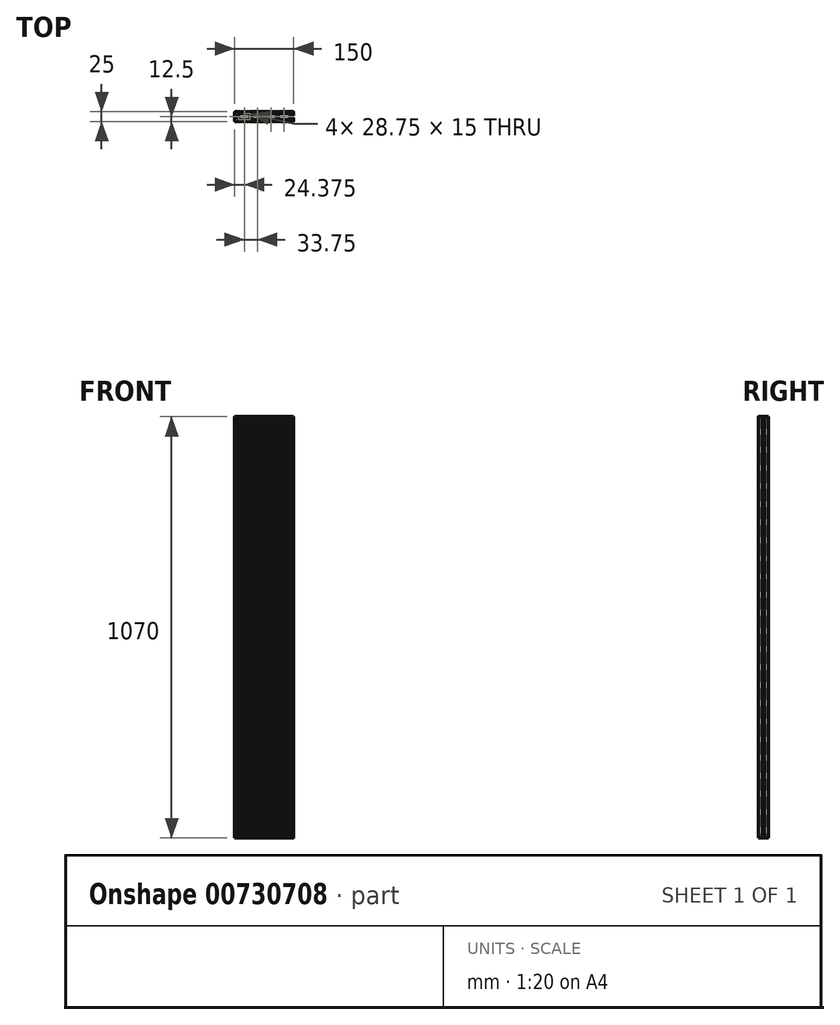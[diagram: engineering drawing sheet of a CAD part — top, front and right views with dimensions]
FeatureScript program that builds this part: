
annotation { "Feature Type Name" : "Feature", "Feature Type Description" : "" }
export const myFeature = defineFeature(function(context is Context, id is Id, definition is map)
    precondition{}
    {
        {
            var Q0;
            Q0=qCreatedBy(makeId("Top.planeOp"),FACE);
            var sketch = newSketch(context, id + "F0", { "sketchPlane" : qUnion([Q0])});
            skLineSegment(sketch, "E0", {"start": v(0, 26.25) * mm, "end": v(0, -33.75) * mm, "construction": true});
            skLineSegment(sketch, "E1", {"start": v(-31.25, 0) * mm, "end": v(28.53, 0) * mm, "construction": true});
            skLineSegment(sketch, "E2", {"start": v(0, 12.5) * mm, "end": v(-75, 12.5) * mm});
            skLineSegment(sketch, "E3", {"start": v(-75, 12.5) * mm, "end": v(-75, 2.5) * mm});
            skLineSegment(sketch, "E4", {"start": v(-75, 2.5) * mm, "end": v(-70, 2.5) * mm});
            skLineSegment(sketch, "E5", {"start": v(-70, 2.5) * mm, "end": v(-70, 0) * mm});
            skLineSegment(sketch, "E6", {"start": v(-65, 0) * mm, "end": v(-65, 7.5) * mm});
            skLineSegment(sketch, "E7", {"start": v(-65, 7.5) * mm, "end": v(-36.25, 7.5) * mm});
            skLineSegment(sketch, "E8", {"start": v(-36.25, 7.5) * mm, "end": v(-36.25, 0) * mm});
            skLineSegment(sketch, "E9", {"start": v(-31.25, 0) * mm, "end": v(-31.25, 7.5) * mm});
            skLineSegment(sketch, "E10", {"start": v(-31.25, 7.5) * mm, "end": v(-2.5, 7.5) * mm});
            skLineSegment(sketch, "E11", {"start": v(-2.5, 7.5) * mm, "end": v(-2.5, 0) * mm});
            skLineSegment(sketch, "E12.MirrorCS", {"start": v(75, 12.5) * mm, "end": v(75, 2.5) * mm});
            skLineSegment(sketch, "E13.MirrorCS", {"start": v(75, 2.5) * mm, "end": v(70, 2.5) * mm});
            skLineSegment(sketch, "E14.MirrorCS", {"start": v(70, 2.5) * mm, "end": v(70, 0) * mm});
            skLineSegment(sketch, "E15.MirrorCS", {"start": v(65, 0) * mm, "end": v(65, 7.5) * mm});
            skLineSegment(sketch, "E16.MirrorCS", {"start": v(65, 7.5) * mm, "end": v(36.25, 7.5) * mm});
            skLineSegment(sketch, "E17.MirrorCS", {"start": v(36.25, 7.5) * mm, "end": v(36.25, 0) * mm});
            skLineSegment(sketch, "E18.MirrorCS", {"start": v(0, 12.5) * mm, "end": v(75, 12.5) * mm});
            skLineSegment(sketch, "E19.MirrorCS", {"start": v(2.5, 7.5) * mm, "end": v(2.5, 0) * mm});
            skLineSegment(sketch, "E20.MirrorCS", {"start": v(31.25, 0) * mm, "end": v(31.25, 7.5) * mm});
            skLineSegment(sketch, "E21.MirrorCS", {"start": v(31.25, 7.5) * mm, "end": v(2.5, 7.5) * mm});
            skLineSegment(sketch, "E22.MirrorCS", {"start": v(70, -2.5) * mm, "end": v(70, 0) * mm});
            skLineSegment(sketch, "E23.MirrorCS", {"start": v(-70, -2.5) * mm, "end": v(-70, 0) * mm});
            skLineSegment(sketch, "E24.MirrorCS", {"start": v(65, 0) * mm, "end": v(65, -7.5) * mm});
            skLineSegment(sketch, "E25.MirrorCS", {"start": v(65, -7.5) * mm, "end": v(36.25, -7.5) * mm});
            skLineSegment(sketch, "E26.MirrorCS", {"start": v(36.25, -7.5) * mm, "end": v(36.25, 0) * mm});
            skLineSegment(sketch, "E27.MirrorCS", {"start": v(75, -2.5) * mm, "end": v(70, -2.5) * mm});
            skLineSegment(sketch, "E28.MirrorCS", {"start": v(0, -12.5) * mm, "end": v(75, -12.5) * mm});
            skLineSegment(sketch, "E29.MirrorCS", {"start": v(2.5, -7.5) * mm, "end": v(2.5, 0) * mm});
            skLineSegment(sketch, "E30.MirrorCS", {"start": v(31.25, 0) * mm, "end": v(31.25, -7.5) * mm});
            skLineSegment(sketch, "E31.MirrorCS", {"start": v(31.25, -7.5) * mm, "end": v(2.5, -7.5) * mm});
            skLineSegment(sketch, "E32.MirrorCS", {"start": v(75, -12.5) * mm, "end": v(75, -2.5) * mm});
            skLineSegment(sketch, "E33.MirrorCS", {"start": v(-2.5, -7.5) * mm, "end": v(-2.5, 0) * mm});
            skLineSegment(sketch, "E34.MirrorCS", {"start": v(-31.25, -7.5) * mm, "end": v(-2.5, -7.5) * mm});
            skLineSegment(sketch, "E35.MirrorCS", {"start": v(-31.25, 0) * mm, "end": v(-31.25, -7.5) * mm});
            skLineSegment(sketch, "E36.MirrorCS", {"start": v(-36.25, -7.5) * mm, "end": v(-36.25, 0) * mm});
            skLineSegment(sketch, "E37.MirrorCS", {"start": v(-65, -7.5) * mm, "end": v(-36.25, -7.5) * mm});
            skLineSegment(sketch, "E38.MirrorCS", {"start": v(-65, 0) * mm, "end": v(-65, -7.5) * mm});
            skLineSegment(sketch, "E39.MirrorCS", {"start": v(0, -12.5) * mm, "end": v(-75, -12.5) * mm});
            skLineSegment(sketch, "E40.MirrorCS", {"start": v(-75, -12.5) * mm, "end": v(-75, -2.5) * mm});
            skLineSegment(sketch, "E41.MirrorCS", {"start": v(-75, -2.5) * mm, "end": v(-70, -2.5) * mm});
            skSolve(sketch);
        }
        {
            var Q0;
            Q0=makeQuery(id+"F0.imprint","IMPRINT",FACE,{"disambiguationData":[TD([[makeQuery(id+"F0.imprint","IMPRINT",EDGE,{"derivedFrom":sQuery(id+"F0.wireOp",EDGE,"E2")}),1.0]])]});
            extrude(context, id + "F1", {"entities" : qUnion([Q0]), "depth" : 1070 * mm, "offsetDistance" : 25 * mm});
        }
        {
            var Q0;
            Q0=makeQuery(id+"F1.opExtrude","SWEPT_EDGE",EDGE,{"disambiguationData":[OSD([sQuery(id+"F0.wireOp",EDGE,"E28.MirrorCS"),sQuery(id+"F0.wireOp",EDGE,"E32.MirrorCS")])]});
            var Q1;
            Q1=makeQuery(id+"F1.opExtrude","SWEPT_EDGE",EDGE,{"disambiguationData":[OSD([sQuery(id+"F0.wireOp",EDGE,"E12.MirrorCS"),sQuery(id+"F0.wireOp",EDGE,"E18.MirrorCS")])]});
            var Q2;
            Q2=makeQuery(id+"F1.opExtrude","SWEPT_EDGE",EDGE,{"disambiguationData":[OSD([sQuery(id+"F0.wireOp",EDGE,"E39.MirrorCS"),sQuery(id+"F0.wireOp",EDGE,"E40.MirrorCS")])]});
            var Q3;
            Q3=makeQuery(id+"F1.opExtrude","SWEPT_EDGE",EDGE,{"disambiguationData":[OSD([sQuery(id+"F0.wireOp",EDGE,"E2"),sQuery(id+"F0.wireOp",EDGE,"E3")])]});
            fillet(context, id + "F2", {"entities" : qUnion([Q0, Q1, Q2, Q3]), "radius" : 2 * mm, "tangentPropagation" : true, "allowEdgeOverflow" : false});
        }
        {
            var Q0;
            Q0=makeQuery(id+"F1.opExtrude","CAP_FACE",FACE,{"disambiguationData":[OSD([sQuery(id+"F0.wireOp",EDGE,"E2"),sQuery(id+"F0.wireOp",EDGE,"E3"),sQuery(id+"F0.wireOp",EDGE,"E4"),sQuery(id+"F0.wireOp",EDGE,"E5"),sQuery(id+"F0.wireOp",EDGE,"E6"),sQuery(id+"F0.wireOp",EDGE,"E7"),sQuery(id+"F0.wireOp",EDGE,"E8"),sQuery(id+"F0.wireOp",EDGE,"E9"),sQuery(id+"F0.wireOp",EDGE,"E10"),sQuery(id+"F0.wireOp",EDGE,"E11"),sQuery(id+"F0.wireOp",EDGE,"E12.MirrorCS"),sQuery(id+"F0.wireOp",EDGE,"E13.MirrorCS"),sQuery(id+"F0.wireOp",EDGE,"E14.MirrorCS"),sQuery(id+"F0.wireOp",EDGE,"E15.MirrorCS"),sQuery(id+"F0.wireOp",EDGE,"E16.MirrorCS"),sQuery(id+"F0.wireOp",EDGE,"E17.MirrorCS"),sQuery(id+"F0.wireOp",EDGE,"E18.MirrorCS"),sQuery(id+"F0.wireOp",EDGE,"E19.MirrorCS"),sQuery(id+"F0.wireOp",EDGE,"E20.MirrorCS"),sQuery(id+"F0.wireOp",EDGE,"E21.MirrorCS"),sQuery(id+"F0.wireOp",EDGE,"E22.MirrorCS"),sQuery(id+"F0.wireOp",EDGE,"E23.MirrorCS"),sQuery(id+"F0.wireOp",EDGE,"E24.MirrorCS"),sQuery(id+"F0.wireOp",EDGE,"E25.MirrorCS"),sQuery(id+"F0.wireOp",EDGE,"E26.MirrorCS"),sQuery(id+"F0.wireOp",EDGE,"E27.MirrorCS"),sQuery(id+"F0.wireOp",EDGE,"E28.MirrorCS"),sQuery(id+"F0.wireOp",EDGE,"E29.MirrorCS"),sQuery(id+"F0.wireOp",EDGE,"E30.MirrorCS"),sQuery(id+"F0.wireOp",EDGE,"E31.MirrorCS"),sQuery(id+"F0.wireOp",EDGE,"E32.MirrorCS"),sQuery(id+"F0.wireOp",EDGE,"E33.MirrorCS"),sQuery(id+"F0.wireOp",EDGE,"E34.MirrorCS"),sQuery(id+"F0.wireOp",EDGE,"E35.MirrorCS"),sQuery(id+"F0.wireOp",EDGE,"E36.MirrorCS"),sQuery(id+"F0.wireOp",EDGE,"E37.MirrorCS"),sQuery(id+"F0.wireOp",EDGE,"E38.MirrorCS"),sQuery(id+"F0.wireOp",EDGE,"E39.MirrorCS"),sQuery(id+"F0.wireOp",EDGE,"E40.MirrorCS"),sQuery(id+"F0.wireOp",EDGE,"E41.MirrorCS")])],"isStart":false});
            var sketch = newSketch(context, id + "F3", { "sketchPlane" : qUnion([Q0])});
            skCircle(sketch, "E42", {"center": v(-65, 12.5) * mm, "radius": 1 * mm});
            skLineSegment(sketch, "E43", {"start": v(-72.39, 0) * mm, "end": v(5.82, 0) * mm, "construction": true});
            skPoint(sketch, "E43.endSnap0", {"position": v(-2.5, 0) * mm});
            skCircle(sketch, "E44", {"center": v(-65, -12.5) * mm, "radius": 1 * mm});
            skCircle(sketch, "E45.1.0.0", {"center": v(-60, 12.5) * mm, "radius": 1 * mm});
            skCircle(sketch, "E45.1.0.1", {"center": v(-60, -12.5) * mm, "radius": 1 * mm});
            skCircle(sketch, "E45.2.0.0", {"center": v(-55, 12.5) * mm, "radius": 1 * mm});
            skCircle(sketch, "E45.2.0.1", {"center": v(-55, -12.5) * mm, "radius": 1 * mm});
            skCircle(sketch, "E45.3.0.0", {"center": v(-50, 12.5) * mm, "radius": 1 * mm});
            skCircle(sketch, "E45.3.0.1", {"center": v(-50, -12.5) * mm, "radius": 1 * mm});
            skCircle(sketch, "E45.4.0.0", {"center": v(-45, 12.5) * mm, "radius": 1 * mm});
            skCircle(sketch, "E45.4.0.1", {"center": v(-45, -12.5) * mm, "radius": 1 * mm});
            skCircle(sketch, "E45.5.0.0", {"center": v(-40, 12.5) * mm, "radius": 1 * mm});
            skCircle(sketch, "E45.5.0.1", {"center": v(-40, -12.5) * mm, "radius": 1 * mm});
            skCircle(sketch, "E45.6.0.0", {"center": v(-35, 12.5) * mm, "radius": 1 * mm});
            skCircle(sketch, "E45.6.0.1", {"center": v(-35, -12.5) * mm, "radius": 1 * mm});
            skCircle(sketch, "E45.7.0.0", {"center": v(-30, 12.5) * mm, "radius": 1 * mm});
            skCircle(sketch, "E45.7.0.1", {"center": v(-30, -12.5) * mm, "radius": 1 * mm});
            skCircle(sketch, "E45.8.0.0", {"center": v(-25, 12.5) * mm, "radius": 1 * mm});
            skCircle(sketch, "E45.8.0.1", {"center": v(-25, -12.5) * mm, "radius": 1 * mm});
            skCircle(sketch, "E45.9.0.0", {"center": v(-20, 12.5) * mm, "radius": 1 * mm});
            skCircle(sketch, "E45.9.0.1", {"center": v(-20, -12.5) * mm, "radius": 1 * mm});
            skCircle(sketch, "E45.10.0.0", {"center": v(-15, 12.5) * mm, "radius": 1 * mm});
            skCircle(sketch, "E45.10.0.1", {"center": v(-15, -12.5) * mm, "radius": 1 * mm});
            skCircle(sketch, "E45.11.0.0", {"center": v(-10, 12.5) * mm, "radius": 1 * mm});
            skCircle(sketch, "E45.11.0.1", {"center": v(-10, -12.5) * mm, "radius": 1 * mm});
            skCircle(sketch, "E45.12.0.0", {"center": v(-5, 12.5) * mm, "radius": 1 * mm});
            skCircle(sketch, "E45.12.0.1", {"center": v(-5, -12.5) * mm, "radius": 1 * mm});
            skCircle(sketch, "E45.13.0.0", {"center": v(0, 12.5) * mm, "radius": 1 * mm});
            skCircle(sketch, "E45.13.0.1", {"center": v(0, -12.5) * mm, "radius": 1 * mm});
            skCircle(sketch, "E45.14.0.0", {"center": v(5, 12.5) * mm, "radius": 1 * mm});
            skCircle(sketch, "E45.14.0.1", {"center": v(5, -12.5) * mm, "radius": 1 * mm});
            skCircle(sketch, "E45.15.0.0", {"center": v(10, 12.5) * mm, "radius": 1 * mm});
            skCircle(sketch, "E45.15.0.1", {"center": v(10, -12.5) * mm, "radius": 1 * mm});
            skCircle(sketch, "E45.16.0.0", {"center": v(15, 12.5) * mm, "radius": 1 * mm});
            skCircle(sketch, "E45.16.0.1", {"center": v(15, -12.5) * mm, "radius": 1 * mm});
            skCircle(sketch, "E45.17.0.0", {"center": v(20, 12.5) * mm, "radius": 1 * mm});
            skCircle(sketch, "E45.17.0.1", {"center": v(20, -12.5) * mm, "radius": 1 * mm});
            skCircle(sketch, "E45.18.0.0", {"center": v(25, 12.5) * mm, "radius": 1 * mm});
            skCircle(sketch, "E45.18.0.1", {"center": v(25, -12.5) * mm, "radius": 1 * mm});
            skCircle(sketch, "E45.19.0.0", {"center": v(30, 12.5) * mm, "radius": 1 * mm});
            skCircle(sketch, "E45.19.0.1", {"center": v(30, -12.5) * mm, "radius": 1 * mm});
            skLineSegment(sketch, "E45.direction1", {"start": v(-65, -12.5) * mm, "end": v(-60, -12.5) * mm, "construction": true});
            skCircle(sketch, "E46.0.20.0", {"center": v(35, 12.5) * mm, "radius": 1 * mm});
            skCircle(sketch, "E46.2.20.0", {"center": v(35, -12.5) * mm, "radius": 1 * mm});
            skCircle(sketch, "E46.0.21.0", {"center": v(40, 12.5) * mm, "radius": 1 * mm});
            skCircle(sketch, "E46.2.21.0", {"center": v(40, -12.5) * mm, "radius": 1 * mm});
            skCircle(sketch, "E46.0.22.0", {"center": v(45, 12.5) * mm, "radius": 1 * mm});
            skCircle(sketch, "E46.2.22.0", {"center": v(45, -12.5) * mm, "radius": 1 * mm});
            skCircle(sketch, "E46.0.23.0", {"center": v(50, 12.5) * mm, "radius": 1 * mm});
            skCircle(sketch, "E46.2.23.0", {"center": v(50, -12.5) * mm, "radius": 1 * mm});
            skCircle(sketch, "E46.0.24.0", {"center": v(55, 12.5) * mm, "radius": 1 * mm});
            skCircle(sketch, "E46.2.24.0", {"center": v(55, -12.5) * mm, "radius": 1 * mm});
            skCircle(sketch, "E46.0.25.0", {"center": v(60, 12.5) * mm, "radius": 1 * mm});
            skCircle(sketch, "E46.2.25.0", {"center": v(60, -12.5) * mm, "radius": 1 * mm});
            skCircle(sketch, "E47.0.26.0", {"center": v(65, 12.5) * mm, "radius": 1 * mm});
            skCircle(sketch, "E47.2.26.0", {"center": v(65, -12.5) * mm, "radius": 1 * mm});
            skSolve(sketch);
        }
        {
            var Q0;
            Q0 = qSketchRegion(id + "F3", true);
            extrude(context, id + "F4", {"entities" : qUnion([Q0]), "operationType" : NewBodyOperationType.REMOVE, "oppositeDirection" : true, "depth" : 1070 * mm, "offsetDistance" : 25 * mm});
        }
    });
